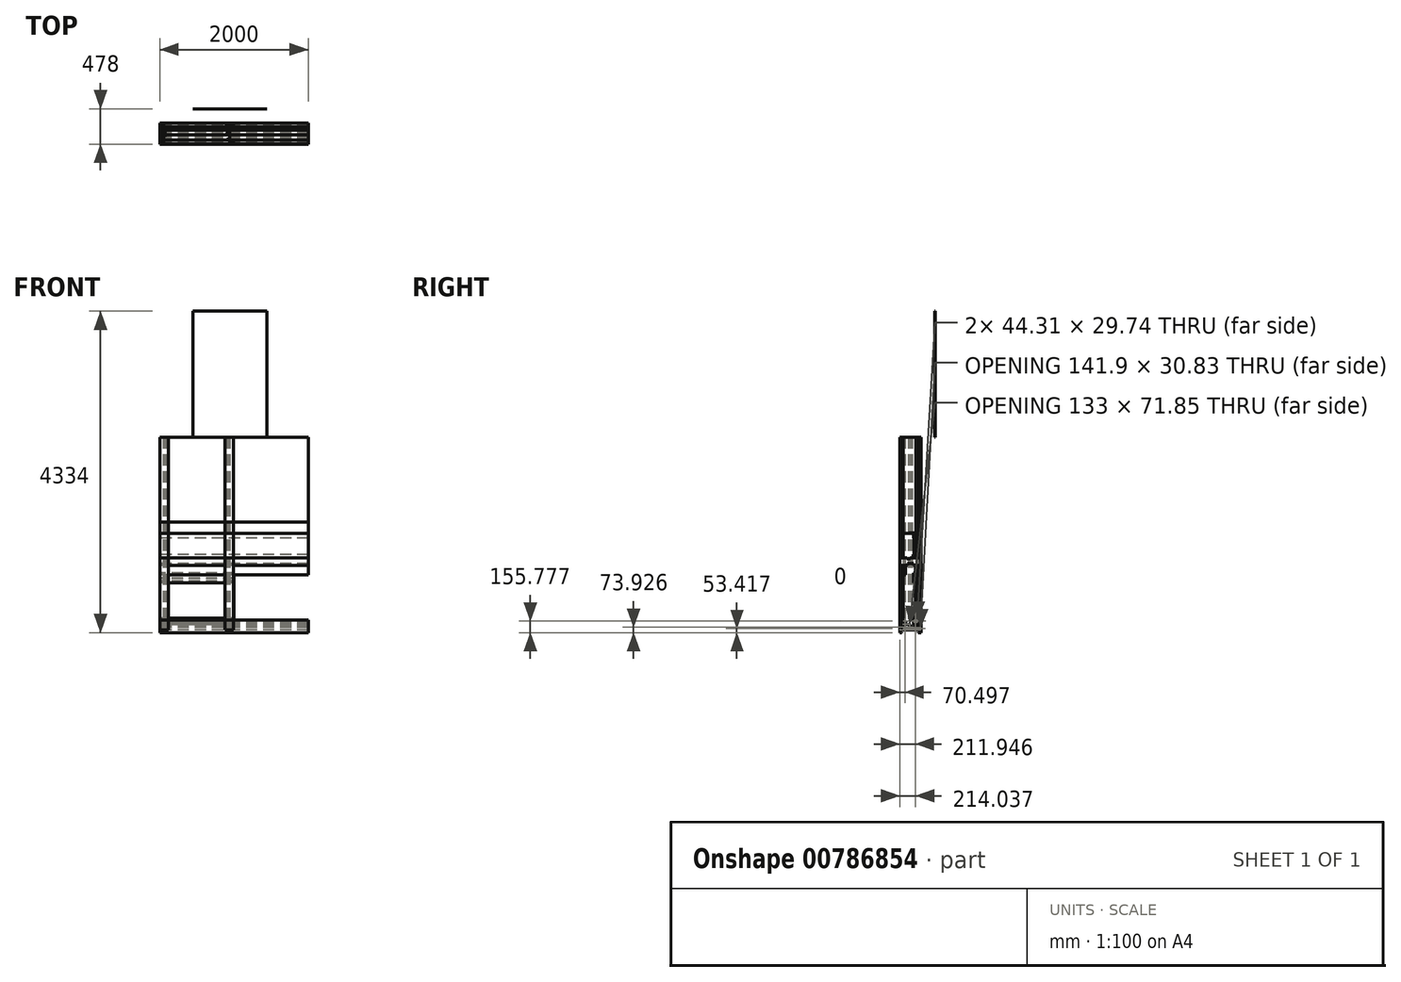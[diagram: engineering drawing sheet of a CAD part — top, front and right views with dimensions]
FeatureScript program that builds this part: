
annotation { "Feature Type Name" : "Feature", "Feature Type Description" : "" }
export const myFeature = defineFeature(function(context is Context, id is Id, definition is map)
    precondition{}
    {
        {
            var Q0;
            Q0=qCreatedBy(makeId("Top.planeOp"),FACE);
            var sketch = newSketch(context, id + "F0", { "sketchPlane" : qUnion([Q0])});
            skLineSegment(sketch, "E0", {"start": v(-131.77, 26.16) * mm, "end": v(-135.77, 26.16) * mm});
            skLineSegment(sketch, "E1", {"start": v(-135.77, 26.16) * mm, "end": v(-135.77, 70.16) * mm});
            skLineSegment(sketch, "E2", {"start": v(-135.77, 70.16) * mm, "end": v(-20.77, 70.16) * mm});
            skLineSegment(sketch, "E3", {"start": v(-20.77, 70.16) * mm, "end": v(-20.77, 66.16) * mm});
            skLineSegment(sketch, "E4", {"start": v(-20.77, 66.16) * mm, "end": v(-84.72, 66.16) * mm});
            skLineSegment(sketch, "E5", {"start": v(-84.72, 66.16) * mm, "end": v(-84.72, 4.73) * mm});
            skLineSegment(sketch, "E6", {"start": v(-84.72, 4.73) * mm, "end": v(-58.72, 4.73) * mm});
            skLineSegment(sketch, "E7", {"start": v(-58.72, 4.73) * mm, "end": v(-58.72, 6.73) * mm});
            skLineSegment(sketch, "E8", {"start": v(-58.72, 6.73) * mm, "end": v(-44.72, 0.73) * mm});
            skLineSegment(sketch, "E9", {"start": v(-44.72, 0.73) * mm, "end": v(-84.72, 0.73) * mm});
            skLineSegment(sketch, "E10", {"start": v(-84.72, 0.73) * mm, "end": v(-84.72, -93.45) * mm});
            skLineSegment(sketch, "E11", {"start": v(-84.72, -93.45) * mm, "end": v(-60.2, -93.45) * mm});
            skLineSegment(sketch, "E12", {"start": v(-60.2, -93.45) * mm, "end": v(-60.2, -73.83) * mm});
            skLineSegment(sketch, "E13", {"start": v(-60.2, -73.83) * mm, "end": v(-44.72, -73.83) * mm});
            skLineSegment(sketch, "E14", {"start": v(-44.72, -73.83) * mm, "end": v(-44.72, -79.83) * mm});
            skLineSegment(sketch, "E15", {"start": v(-44.72, -79.83) * mm, "end": v(-48.72, -79.83) * mm});
            skLineSegment(sketch, "E16", {"start": v(-48.72, -79.83) * mm, "end": v(-48.72, -77.83) * mm});
            skLineSegment(sketch, "E17", {"start": v(-48.72, -77.83) * mm, "end": v(-56.2, -77.83) * mm});
            skLineSegment(sketch, "E18", {"start": v(-56.2, -77.83) * mm, "end": v(-56.2, -93.45) * mm});
            skLineSegment(sketch, "E19", {"start": v(-56.2, -93.45) * mm, "end": v(-48.72, -93.45) * mm});
            skLineSegment(sketch, "E20", {"start": v(-48.72, -93.45) * mm, "end": v(-48.72, -91.45) * mm});
            skLineSegment(sketch, "E21", {"start": v(-48.72, -91.45) * mm, "end": v(-44.72, -91.45) * mm});
            skLineSegment(sketch, "E22", {"start": v(-44.72, -91.45) * mm, "end": v(-44.72, -97.45) * mm});
            skLineSegment(sketch, "E23", {"start": v(-44.72, -97.45) * mm, "end": v(-84.72, -97.45) * mm});
            skLineSegment(sketch, "E24", {"start": v(-84.72, -97.45) * mm, "end": v(-84.72, -212.73) * mm});
            skLineSegment(sketch, "E25", {"start": v(-84.72, -212.73) * mm, "end": v(-20.77, -212.73) * mm});
            skLineSegment(sketch, "E26", {"start": v(-20.77, -212.73) * mm, "end": v(-20.77, -216.73) * mm});
            skLineSegment(sketch, "E27", {"start": v(-20.77, -216.73) * mm, "end": v(-135.77, -216.73) * mm});
            skLineSegment(sketch, "E28", {"start": v(-135.77, -216.73) * mm, "end": v(-135.77, -172.73) * mm});
            skLineSegment(sketch, "E29", {"start": v(-135.77, -172.73) * mm, "end": v(-131.77, -172.73) * mm});
            skLineSegment(sketch, "E30", {"start": v(-131.77, -172.73) * mm, "end": v(-131.77, -212.73) * mm});
            skLineSegment(sketch, "E31", {"start": v(-131.77, -212.73) * mm, "end": v(-88.72, -212.73) * mm});
            skLineSegment(sketch, "E32", {"start": v(-88.72, -212.73) * mm, "end": v(-88.72, 66.16) * mm});
            skLineSegment(sketch, "E33", {"start": v(-88.72, 66.16) * mm, "end": v(-131.77, 66.16) * mm});
            skLineSegment(sketch, "E34", {"start": v(-131.77, 66.16) * mm, "end": v(-131.77, 26.16) * mm});
            skLineSegment(sketch, "E35.MirrorCS", {"start": v(763.76, -72.74) * mm, "end": v(763.76, -66.74) * mm});
            skLineSegment(sketch, "E36.MirrorCS", {"start": v(767.76, -66.74) * mm, "end": v(767.76, -68.74) * mm});
            skLineSegment(sketch, "E37.MirrorCS", {"start": v(767.76, -68.74) * mm, "end": v(775.23, -68.74) * mm});
            skLineSegment(sketch, "E38.MirrorCS", {"start": v(775.23, -68.74) * mm, "end": v(775.23, -53.12) * mm});
            skLineSegment(sketch, "E39.MirrorCS", {"start": v(779.23, -72.74) * mm, "end": v(763.76, -72.74) * mm});
            skLineSegment(sketch, "E40.MirrorCS", {"start": v(767.76, -53.12) * mm, "end": v(767.76, -55.12) * mm});
            skLineSegment(sketch, "E41.MirrorCS", {"start": v(763.76, -66.74) * mm, "end": v(767.76, -66.74) * mm});
            skLineSegment(sketch, "E42.MirrorCS", {"start": v(767.76, -55.12) * mm, "end": v(763.76, -55.12) * mm});
            skLineSegment(sketch, "E43.MirrorCS", {"start": v(763.76, -55.12) * mm, "end": v(763.76, -49.12) * mm});
            skLineSegment(sketch, "E44.MirrorCS", {"start": v(775.23, -53.12) * mm, "end": v(767.76, -53.12) * mm});
            skLineSegment(sketch, "E45.MirrorCS", {"start": v(779.23, -53.12) * mm, "end": v(779.23, -72.74) * mm});
            skLineSegment(sketch, "E46.MirrorCS", {"start": v(763.76, -49.12) * mm, "end": v(803.76, -49.12) * mm});
            skLineSegment(sketch, "E47.MirrorCS", {"start": v(803.76, -53.12) * mm, "end": v(779.23, -53.12) * mm});
            skLineSegment(sketch, "E48.MirrorCS", {"start": v(777.76, -153.3) * mm, "end": v(763.76, -147.3) * mm});
            skLineSegment(sketch, "E49.MirrorCS", {"start": v(850.81, -172.73) * mm, "end": v(854.81, -172.73) * mm});
            skLineSegment(sketch, "E50.MirrorCS", {"start": v(803.76, -151.3) * mm, "end": v(777.76, -151.3) * mm});
            skLineSegment(sketch, "E51.MirrorCS", {"start": v(777.76, -151.3) * mm, "end": v(777.76, -153.3) * mm});
            skLineSegment(sketch, "E52.MirrorCS", {"start": v(763.76, -147.3) * mm, "end": v(803.76, -147.3) * mm});
            skLineSegment(sketch, "E53.MirrorCS", {"start": v(739.81, -216.73) * mm, "end": v(739.81, -212.73) * mm});
            skLineSegment(sketch, "E54.MirrorCS", {"start": v(854.81, -0.01) * mm, "end": v(850.81, -0.01) * mm});
            skLineSegment(sketch, "E55.MirrorCS", {"start": v(739.81, 39.99) * mm, "end": v(739.81, 43.99) * mm});
            skLineSegment(sketch, "E56.MirrorCS", {"start": v(850.81, 39.99) * mm, "end": v(807.76, 39.99) * mm});
            skLineSegment(sketch, "E57.MirrorCS", {"start": v(803.76, -49.12) * mm, "end": v(803.76, 39.99) * mm});
            skLineSegment(sketch, "E58.MirrorCS", {"start": v(854.81, -172.73) * mm, "end": v(854.81, -216.73) * mm});
            skLineSegment(sketch, "E59.MirrorCS", {"start": v(807.76, -212.73) * mm, "end": v(850.81, -212.73) * mm});
            skLineSegment(sketch, "E60.MirrorCS", {"start": v(850.81, -0.01) * mm, "end": v(850.81, 39.99) * mm});
            skLineSegment(sketch, "E61.MirrorCS", {"start": v(854.81, -216.73) * mm, "end": v(739.81, -216.73) * mm});
            skLineSegment(sketch, "E62.MirrorCS", {"start": v(850.81, -212.73) * mm, "end": v(850.81, -172.73) * mm});
            skLineSegment(sketch, "E63.MirrorCS", {"start": v(803.76, 39.99) * mm, "end": v(739.81, 39.99) * mm});
            skLineSegment(sketch, "E64.MirrorCS", {"start": v(803.76, -147.3) * mm, "end": v(803.76, -53.12) * mm});
            skLineSegment(sketch, "E65.MirrorCS", {"start": v(803.76, -212.73) * mm, "end": v(803.76, -151.3) * mm});
            skLineSegment(sketch, "E66.MirrorCS", {"start": v(739.81, -212.73) * mm, "end": v(803.76, -212.73) * mm});
            skLineSegment(sketch, "E67.MirrorCS", {"start": v(854.81, 43.99) * mm, "end": v(854.81, -0.01) * mm});
            skLineSegment(sketch, "E68.MirrorCS", {"start": v(807.76, 39.99) * mm, "end": v(807.76, -212.73) * mm});
            skLineSegment(sketch, "E69.MirrorCS", {"start": v(739.81, 43.99) * mm, "end": v(854.81, 43.99) * mm});
            skSolve(sketch);
        }
        {
            var Q0;
            Q0=makeQuery(id+"F0.imprint","IMPRINT",FACE,{"disambiguationData":[TD([[makeQuery(id+"F0.imprint","IMPRINT",EDGE,{"derivedFrom":sQuery(id+"F0.wireOp",EDGE,"E0")}),-1.0]])]});
            extrude(context, id + "F1", {"entities" : qUnion([Q0]), "depth" : 2600 * mm, "offsetDistance" : 25 * mm});
        }
        {
            var Q0;
            Q0=makeQuery(id+"F0.imprint","IMPRINT",FACE,{"disambiguationData":[TD([[makeQuery(id+"F0.imprint","IMPRINT",EDGE,{"derivedFrom":sQuery(id+"F0.wireOp",EDGE,"E35.MirrorCS")}),-1.0]])]});
            extrude(context, id + "F2", {"entities" : qUnion([Q0]), "depth" : 2600 * mm, "offsetDistance" : 25 * mm});
        }
        {
            var Q0;
            Q0=makeQuery(id+"F1.opExtrude","SWEPT_FACE",FACE,{"disambiguationData":[OSD([sQuery(id+"F0.wireOp",EDGE,"E28")])]});
            var sketch = newSketch(context, id + "F3", { "sketchPlane" : qUnion([Q0])});
            skLineSegment(sketch, "E70", {"start": v(-70.16, -34) * mm, "end": v(-70.16, 69.03) * mm});
            skLineSegment(sketch, "E71", {"start": v(-70.16, 69.03) * mm, "end": v(-66.16, 69.03) * mm});
            skLineSegment(sketch, "E72", {"start": v(-66.16, 69.03) * mm, "end": v(-66.16, 36.25) * mm});
            skLineSegment(sketch, "E73", {"start": v(-66.16, 36.25) * mm, "end": v(-11.46, 36.25) * mm});
            skLineSegment(sketch, "E74", {"start": v(0, 38.83) * mm, "end": v(0, 88.3) * mm});
            skLineSegment(sketch, "E75", {"start": v(0, 88.3) * mm, "end": v(-6.87, 88.3) * mm});
            skLineSegment(sketch, "E76", {"start": v(-6.87, 88.3) * mm, "end": v(-6.87, 76.3) * mm});
            skLineSegment(sketch, "E77", {"start": v(-6.87, 76.3) * mm, "end": v(-11.46, 76.3) * mm});
            skLineSegment(sketch, "E78", {"start": v(-11.46, 76.3) * mm, "end": v(-11.46, 92.3) * mm});
            skLineSegment(sketch, "E79", {"start": v(-11.46, 92.3) * mm, "end": v(16.85, 92.3) * mm});
            skLineSegment(sketch, "E80", {"start": v(16.85, 92.3) * mm, "end": v(16.85, 76.3) * mm});
            skLineSegment(sketch, "E81", {"start": v(16.85, 76.3) * mm, "end": v(12.85, 76.3) * mm});
            skLineSegment(sketch, "E82", {"start": v(12.85, 76.3) * mm, "end": v(12.85, 88.3) * mm});
            skLineSegment(sketch, "E83", {"start": v(12.85, 88.3) * mm, "end": v(4, 88.3) * mm});
            skLineSegment(sketch, "E84", {"start": v(4, 88.3) * mm, "end": v(4, 38.83) * mm});
            skLineSegment(sketch, "E85", {"start": v(-70.16, -34) * mm, "end": v(-32.13, -34) * mm});
            skLineSegment(sketch, "E86", {"start": v(-32.13, -34) * mm, "end": v(-32.13, -30) * mm});
            skLineSegment(sketch, "E87", {"start": v(-32.13, -30) * mm, "end": v(-66.16, -30) * mm});
            skLineSegment(sketch, "E88", {"start": v(-66.16, -30) * mm, "end": v(-66.16, 0) * mm});
            skLineSegment(sketch, "E89", {"start": v(-66.16, 0) * mm, "end": v(212.73, 0) * mm});
            skLineSegment(sketch, "E90", {"start": v(212.73, -30) * mm, "end": v(187.57, -30) * mm});
            skLineSegment(sketch, "E91", {"start": v(187.57, -30) * mm, "end": v(187.57, -34) * mm});
            skLineSegment(sketch, "E92", {"start": v(187.57, -34) * mm, "end": v(216.73, -34) * mm});
            skLineSegment(sketch, "E93", {"start": v(216.73, -34) * mm, "end": v(216.73, 138.64) * mm});
            skLineSegment(sketch, "E94", {"start": v(216.73, 138.64) * mm, "end": v(212.73, 138.64) * mm});
            skLineSegment(sketch, "E95", {"start": v(212.73, 138.64) * mm, "end": v(212.73, 113.43) * mm});
            skLineSegment(sketch, "E96", {"start": v(212.73, 113.43) * mm, "end": v(206.73, 113.43) * mm});
            skLineSegment(sketch, "E97", {"start": v(206.73, 113.43) * mm, "end": v(206.73, 107.43) * mm});
            skLineSegment(sketch, "E98", {"start": v(206.73, 107.43) * mm, "end": v(210.73, 107.43) * mm});
            skLineSegment(sketch, "E99", {"start": v(210.73, 107.43) * mm, "end": v(210.73, 109.43) * mm});
            skLineSegment(sketch, "E100", {"start": v(210.73, 109.43) * mm, "end": v(212.73, 109.43) * mm});
            skLineSegment(sketch, "E101", {"start": v(212.73, 109.43) * mm, "end": v(212.73, 88) * mm});
            skLineSegment(sketch, "E102", {"start": v(212.73, 88) * mm, "end": v(210.73, 88) * mm});
            skLineSegment(sketch, "E103", {"start": v(210.73, 88) * mm, "end": v(210.73, 90) * mm});
            skLineSegment(sketch, "E104", {"start": v(210.73, 90) * mm, "end": v(206.73, 90) * mm});
            skLineSegment(sketch, "E105", {"start": v(206.73, 90) * mm, "end": v(206.73, 84) * mm});
            skLineSegment(sketch, "E106", {"start": v(206.73, 84) * mm, "end": v(212.73, 84) * mm});
            skLineSegment(sketch, "E107", {"start": v(212.73, 84) * mm, "end": v(212.73, 79.86) * mm});
            skLineSegment(sketch, "E108", {"start": v(212.73, -30) * mm, "end": v(212.73, 0) * mm});
            skLineSegment(sketch, "E109", {"start": v(212.73, 4) * mm, "end": v(79.73, 4) * mm});
            skLineSegment(sketch, "E110", {"start": v(72.84, 551.08) * mm, "end": v(72.84, 267.71) * mm, "construction": true});
            skLineSegment(sketch, "E111", {"start": v(146.73, 79.86) * mm, "end": v(146.73, 115.55) * mm});
            skLineSegment(sketch, "E112", {"start": v(150.73, 115.55) * mm, "end": v(150.73, 103.55) * mm});
            skLineSegment(sketch, "E113", {"start": v(150.73, 103.55) * mm, "end": v(154.73, 103.55) * mm});
            skLineSegment(sketch, "E114", {"start": v(154.73, 103.55) * mm, "end": v(154.73, 119.55) * mm});
            skLineSegment(sketch, "E115", {"start": v(154.73, 119.55) * mm, "end": v(134.73, 119.55) * mm});
            skLineSegment(sketch, "E116", {"start": v(134.73, 119.55) * mm, "end": v(134.73, 103.55) * mm});
            skLineSegment(sketch, "E117", {"start": v(134.73, 103.55) * mm, "end": v(138.73, 103.55) * mm});
            skLineSegment(sketch, "E118", {"start": v(138.73, 103.55) * mm, "end": v(138.73, 115.55) * mm});
            skLineSegment(sketch, "E119", {"start": v(138.73, 115.55) * mm, "end": v(142.73, 115.55) * mm});
            skLineSegment(sketch, "E120", {"start": v(142.73, 115.55) * mm, "end": v(142.73, 79.86) * mm});
            skLineSegment(sketch, "E121", {"start": v(142.73, 79.86) * mm, "end": v(67.73, 74.54) * mm});
            skLineSegment(sketch, "E122", {"start": v(67.73, 74.54) * mm, "end": v(67.73, 62.44) * mm});
            skLineSegment(sketch, "E123", {"start": v(67.73, 62.44) * mm, "end": v(71.73, 62.44) * mm});
            skLineSegment(sketch, "E124", {"start": v(71.73, 62.44) * mm, "end": v(71.73, 66.44) * mm});
            skLineSegment(sketch, "E125", {"start": v(71.73, 66.44) * mm, "end": v(75.73, 66.44) * mm});
            skLineSegment(sketch, "E126", {"start": v(75.73, 66.44) * mm, "end": v(75.73, 50.83) * mm});
            skLineSegment(sketch, "E127", {"start": v(75.73, 50.83) * mm, "end": v(71.73, 50.83) * mm});
            skLineSegment(sketch, "E128", {"start": v(71.73, 50.83) * mm, "end": v(71.73, 54.83) * mm});
            skLineSegment(sketch, "E129", {"start": v(71.73, 54.83) * mm, "end": v(67.73, 54.83) * mm});
            skLineSegment(sketch, "E130", {"start": v(67.73, 54.83) * mm, "end": v(67.73, 46.83) * mm});
            skLineSegment(sketch, "E131", {"start": v(67.73, 46.83) * mm, "end": v(75.73, 46.83) * mm});
            skLineSegment(sketch, "E132", {"start": v(75.73, 46.83) * mm, "end": v(75.73, 38.83) * mm});
            skLineSegment(sketch, "E133", {"start": v(75.73, 38.83) * mm, "end": v(4, 38.83) * mm});
            skLineSegment(sketch, "E134", {"start": v(146.73, 115.55) * mm, "end": v(150.73, 115.55) * mm});
            skLineSegment(sketch, "E135", {"start": v(146.73, 79.86) * mm, "end": v(212.73, 79.86) * mm});
            skLineSegment(sketch, "E136", {"start": v(212.73, 75.85) * mm, "end": v(142.73, 75.85) * mm});
            skLineSegment(sketch, "E137.trimOffspring", {"start": v(212.73, 75.85) * mm, "end": v(212.73, 4) * mm});
            skLineSegment(sketch, "E138", {"start": v(79.73, 71.38) * mm, "end": v(79.73, 4) * mm});
            skLineSegment(sketch, "E139", {"start": v(142.73, 75.85) * mm, "end": v(79.73, 71.38) * mm});
            skLineSegment(sketch, "E140", {"start": v(75.73, 4) * mm, "end": v(75.73, 34.83) * mm});
            skLineSegment(sketch, "E141", {"start": v(75.73, 34.83) * mm, "end": v(-0.59, 34.83) * mm});
            skLineSegment(sketch, "E142", {"start": v(-12.05, 32.25) * mm, "end": v(-66.16, 32.25) * mm});
            skLineSegment(sketch, "E143", {"start": v(-66.16, 32.25) * mm, "end": v(-66.16, 4) * mm});
            skLineSegment(sketch, "E144", {"start": v(-66.16, 4) * mm, "end": v(75.73, 4) * mm});
            skLineSegment(sketch, "E145", {"start": v(-11.46, 36.25) * mm, "end": v(0, 38.83) * mm});
            skLineSegment(sketch, "E146", {"start": v(-12.05, 32.25) * mm, "end": v(-0.59, 34.83) * mm});
            skSolve(sketch);
        }
        {
            var Q0;
            Q0=qSketchRegion(id+"F3",true);
            extrude(context, id + "F4", {"entities" : qUnion([Q0]), "oppositeDirection" : true, "depth" : 2000 * mm, "offsetDistance" : 25 * mm});
        }
        {
            var Q0;
            Q0=makeQuery(id+"F1.opExtrude","SWEPT_FACE",FACE,{"disambiguationData":[OSD([sQuery(id+"F0.wireOp",EDGE,"E1")])]});
            var sketch = newSketch(context, id + "F5", { "sketchPlane" : qUnion([Q0])});
            skLineSegment(sketch, "E147", {"start": v(-70.16, 972.5) * mm, "end": v(-70.16, 2600) * mm});
            skLineSegment(sketch, "E148", {"start": v(-70.16, 972.5) * mm, "end": v(-14.46, 972.5) * mm});
            skLineSegment(sketch, "E149", {"start": v(-14.46, 972.5) * mm, "end": v(-14.46, 1017.43) * mm});
            skLineSegment(sketch, "E150", {"start": v(-14.46, 1017.43) * mm, "end": v(-10.46, 1017.43) * mm});
            skLineSegment(sketch, "E151", {"start": v(-10.46, 1017.43) * mm, "end": v(-10.46, 972.5) * mm});
            skLineSegment(sketch, "E152", {"start": v(-10.46, 972.5) * mm, "end": v(30.91, 972.5) * mm});
            skLineSegment(sketch, "E153", {"start": v(72.28, 972.5) * mm, "end": v(72.28, 964.5) * mm});
            skLineSegment(sketch, "E154", {"start": v(72.28, 964.5) * mm, "end": v(116.6, 964.5) * mm});
            skLineSegment(sketch, "E155", {"start": v(116.6, 964.5) * mm, "end": v(116.6, 972.5) * mm});
            skLineSegment(sketch, "E156", {"start": v(116.6, 972.5) * mm, "end": v(216.73, 972.5) * mm});
            skLineSegment(sketch, "E157", {"start": v(216.73, 2600) * mm, "end": v(216.73, 972.5) * mm});
            skLineSegment(sketch, "E158", {"start": v(-70.16, 2600) * mm, "end": v(-66.16, 2600) * mm});
            skLineSegment(sketch, "E159", {"start": v(-66.16, 875.29) * mm, "end": v(-66.16, 2600) * mm});
            skLineSegment(sketch, "E160", {"start": v(-66.16, 875.29) * mm, "end": v(1.84, 875.29) * mm});
            skLineSegment(sketch, "E161", {"start": v(1.84, 875.29) * mm, "end": v(1.84, 748.56) * mm});
            skLineSegment(sketch, "E162", {"start": v(1.84, 748.56) * mm, "end": v(5.84, 748.56) * mm});
            skLineSegment(sketch, "E163", {"start": v(5.84, 748.56) * mm, "end": v(5.84, 875.29) * mm});
            skLineSegment(sketch, "E164", {"start": v(5.84, 875.29) * mm, "end": v(33.47, 875.29) * mm});
            skLineSegment(sketch, "E165", {"start": v(33.47, 875.29) * mm, "end": v(33.47, 898.4) * mm});
            skLineSegment(sketch, "E166", {"start": v(33.47, 898.4) * mm, "end": v(112.2, 898.4) * mm});
            skLineSegment(sketch, "E167", {"start": v(30.91, 972.5) * mm, "end": v(30.91, 1017.1) * mm});
            skLineSegment(sketch, "E168", {"start": v(30.91, 1017.1) * mm, "end": v(34.91, 1017.1) * mm});
            skLineSegment(sketch, "E169", {"start": v(34.91, 1017.1) * mm, "end": v(34.91, 972.5) * mm});
            skLineSegment(sketch, "E170.trimOffspring", {"start": v(34.91, 972.5) * mm, "end": v(72.28, 972.5) * mm});
            skLineSegment(sketch, "E171", {"start": v(-66.16, 879.29) * mm, "end": v(-66.16, 968.5) * mm});
            skLineSegment(sketch, "E172", {"start": v(-66.16, 968.5) * mm, "end": v(68.28, 968.5) * mm});
            skLineSegment(sketch, "E173", {"start": v(68.28, 968.5) * mm, "end": v(68.28, 960.5) * mm});
            skLineSegment(sketch, "E174", {"start": v(68.28, 960.5) * mm, "end": v(120.6, 960.5) * mm});
            skLineSegment(sketch, "E175", {"start": v(120.6, 960.5) * mm, "end": v(120.6, 966.67) * mm});
            skLineSegment(sketch, "E176", {"start": v(120.6, 966.67) * mm, "end": v(212.73, 966.67) * mm});
            skLineSegment(sketch, "E177", {"start": v(212.73, 966.67) * mm, "end": v(212.73, 879.29) * mm});
            skLineSegment(sketch, "E178", {"start": v(-66.16, 879.29) * mm, "end": v(29.47, 879.29) * mm});
            skLineSegment(sketch, "E179", {"start": v(29.47, 879.29) * mm, "end": v(29.47, 902.4) * mm});
            skLineSegment(sketch, "E180", {"start": v(29.47, 902.4) * mm, "end": v(116.2, 902.4) * mm});
            skLineSegment(sketch, "E181.MirrorCS", {"start": v(112.2, 875.29) * mm, "end": v(112.2, 898.4) * mm});
            skLineSegment(sketch, "E182.MirrorCS", {"start": v(116.2, 879.29) * mm, "end": v(116.2, 902.4) * mm});
            skLineSegment(sketch, "E183.MirrorCS", {"start": v(211.84, 879.29) * mm, "end": v(116.2, 879.29) * mm});
            skLineSegment(sketch, "E184.MirrorCS", {"start": v(211.84, 875.29) * mm, "end": v(143.84, 875.29) * mm});
            skLineSegment(sketch, "E185.MirrorCS", {"start": v(143.84, 748.56) * mm, "end": v(139.84, 748.56) * mm});
            skLineSegment(sketch, "E186.MirrorCS", {"start": v(139.84, 748.56) * mm, "end": v(139.84, 875.29) * mm});
            skLineSegment(sketch, "E187.MirrorCS", {"start": v(143.84, 875.29) * mm, "end": v(143.84, 748.56) * mm});
            skLineSegment(sketch, "E188.MirrorCS", {"start": v(139.84, 875.29) * mm, "end": v(112.2, 875.29) * mm});
            skLineSegment(sketch, "E189", {"start": v(216.73, 2600) * mm, "end": v(212.73, 2600) * mm});
            skLineSegment(sketch, "E190", {"start": v(212.73, 875.29) * mm, "end": v(212.73, 2600) * mm});
            skLineSegment(sketch, "E191", {"start": v(211.84, 879.29) * mm, "end": v(212.73, 879.29) * mm});
            skLineSegment(sketch, "E192", {"start": v(211.84, 875.29) * mm, "end": v(212.73, 875.29) * mm});
            skSolve(sketch);
        }
        {
            var Q0;
            Q0=qSketchRegion(id+"F5",true);
            extrude(context, id + "F6", {"entities" : qUnion([Q0]), "oppositeDirection" : true, "depth" : 2000 * mm, "offsetDistance" : 25 * mm});
        }
        {
            var Q0;
            Q0=makeQuery(id+"F6.opExtrude","CAP_FACE",FACE,{"disambiguationData":[OSD([sQuery(id+"F5.wireOp",EDGE,"E147"),sQuery(id+"F5.wireOp",EDGE,"E148"),sQuery(id+"F5.wireOp",EDGE,"E149"),sQuery(id+"F5.wireOp",EDGE,"E150"),sQuery(id+"F5.wireOp",EDGE,"E151"),sQuery(id+"F5.wireOp",EDGE,"E152"),sQuery(id+"F5.wireOp",EDGE,"E153"),sQuery(id+"F5.wireOp",EDGE,"E154"),sQuery(id+"F5.wireOp",EDGE,"E155"),sQuery(id+"F5.wireOp",EDGE,"E156"),sQuery(id+"F5.wireOp",EDGE,"E157"),sQuery(id+"F5.wireOp",EDGE,"E158"),sQuery(id+"F5.wireOp",EDGE,"E159"),sQuery(id+"F5.wireOp",EDGE,"E160"),sQuery(id+"F5.wireOp",EDGE,"E161"),sQuery(id+"F5.wireOp",EDGE,"E162"),sQuery(id+"F5.wireOp",EDGE,"E163"),sQuery(id+"F5.wireOp",EDGE,"E164"),sQuery(id+"F5.wireOp",EDGE,"E165"),sQuery(id+"F5.wireOp",EDGE,"E166"),sQuery(id+"F5.wireOp",EDGE,"E167"),sQuery(id+"F5.wireOp",EDGE,"E168"),sQuery(id+"F5.wireOp",EDGE,"E169"),sQuery(id+"F5.wireOp",EDGE,"E170.trimOffspring"),sQuery(id+"F5.wireOp",EDGE,"E171"),sQuery(id+"F5.wireOp",EDGE,"E172"),sQuery(id+"F5.wireOp",EDGE,"E173"),sQuery(id+"F5.wireOp",EDGE,"E174"),sQuery(id+"F5.wireOp",EDGE,"E175"),sQuery(id+"F5.wireOp",EDGE,"E176"),sQuery(id+"F5.wireOp",EDGE,"E177"),sQuery(id+"F5.wireOp",EDGE,"E178"),sQuery(id+"F5.wireOp",EDGE,"E179"),sQuery(id+"F5.wireOp",EDGE,"E180"),sQuery(id+"F5.wireOp",EDGE,"E181.MirrorCS"),sQuery(id+"F5.wireOp",EDGE,"E182.MirrorCS"),sQuery(id+"F5.wireOp",EDGE,"E183.MirrorCS"),sQuery(id+"F5.wireOp",EDGE,"E184.MirrorCS"),sQuery(id+"F5.wireOp",EDGE,"E185.MirrorCS"),sQuery(id+"F5.wireOp",EDGE,"E186.MirrorCS"),sQuery(id+"F5.wireOp",EDGE,"E187.MirrorCS"),sQuery(id+"F5.wireOp",EDGE,"E188.MirrorCS"),sQuery(id+"F5.wireOp",EDGE,"E189"),sQuery(id+"F5.wireOp",EDGE,"E190"),sQuery(id+"F5.wireOp",EDGE,"E191"),sQuery(id+"F5.wireOp",EDGE,"E192")])],"isStart":true});
            var sketch = newSketch(context, id + "F7", { "sketchPlane" : qUnion([Q0])});
            skLineSegment(sketch, "E193", {"start": v(-10.46, 1243.09) * mm, "end": v(-10.46, 1302.74) * mm});
            skLineSegment(sketch, "E194", {"start": v(-10.46, 1302.74) * mm, "end": v(26.58, 1302.74) * mm});
            skLineSegment(sketch, "E195", {"start": v(30.91, 1302.74) * mm, "end": v(30.91, 1306.74) * mm});
            skLineSegment(sketch, "E196", {"start": v(30.91, 1306.74) * mm, "end": v(87.31, 1306.74) * mm});
            skLineSegment(sketch, "E197", {"start": v(87.31, 1306.74) * mm, "end": v(87.31, 1302.74) * mm});
            skLineSegment(sketch, "E198", {"start": v(87.31, 1302.74) * mm, "end": v(216.73, 1302.74) * mm});
            skLineSegment(sketch, "E199", {"start": v(216.73, 1302.74) * mm, "end": v(216.73, 1459.6) * mm});
            skLineSegment(sketch, "E200", {"start": v(216.73, 1459.6) * mm, "end": v(160.6, 1459.6) * mm});
            skLineSegment(sketch, "E201", {"start": v(160.6, 1459.6) * mm, "end": v(160.6, 1455.6) * mm});
            skLineSegment(sketch, "E202", {"start": v(160.6, 1455.6) * mm, "end": v(212.73, 1455.6) * mm});
            skLineSegment(sketch, "E203", {"start": v(212.73, 1455.6) * mm, "end": v(212.73, 1306.74) * mm});
            skLineSegment(sketch, "E204", {"start": v(212.73, 1306.74) * mm, "end": v(91.31, 1306.74) * mm});
            skLineSegment(sketch, "E205", {"start": v(91.31, 1306.74) * mm, "end": v(91.31, 1310.74) * mm});
            skLineSegment(sketch, "E206", {"start": v(91.31, 1310.74) * mm, "end": v(26.91, 1310.74) * mm});
            skLineSegment(sketch, "E207", {"start": v(26.91, 1310.74) * mm, "end": v(26.91, 1306.74) * mm});
            skLineSegment(sketch, "E208", {"start": v(30.91, 1243.09) * mm, "end": v(30.91, 1302.74) * mm});
            skLineSegment(sketch, "E209", {"start": v(-10.46, 1243.09) * mm, "end": v(-14.46, 1243.09) * mm});
            skLineSegment(sketch, "E210", {"start": v(-14.46, 1243.09) * mm, "end": v(-14.46, 1302.74) * mm});
            skLineSegment(sketch, "E211", {"start": v(-14.46, 1302.74) * mm, "end": v(-70.16, 1302.74) * mm});
            skLineSegment(sketch, "E212", {"start": v(-70.16, 1302.74) * mm, "end": v(-70.16, 1458.04) * mm});
            skLineSegment(sketch, "E213", {"start": v(-70.16, 1458.04) * mm, "end": v(-14.46, 1458.04) * mm});
            skLineSegment(sketch, "E214", {"start": v(-14.46, 1458.04) * mm, "end": v(-14.46, 1454.04) * mm});
            skLineSegment(sketch, "E215", {"start": v(-14.46, 1454.04) * mm, "end": v(-66.16, 1454.04) * mm});
            skLineSegment(sketch, "E216", {"start": v(-66.16, 1454.04) * mm, "end": v(-66.16, 1306.74) * mm});
            skLineSegment(sketch, "E217", {"start": v(-66.16, 1306.74) * mm, "end": v(0, 1306.74) * mm});
            skLineSegment(sketch, "E218", {"start": v(0, 1306.74) * mm, "end": v(26.91, 1306.74) * mm});
            skLineSegment(sketch, "E219", {"start": v(30.91, 1243.09) * mm, "end": v(26.58, 1243.09) * mm});
            skLineSegment(sketch, "E220", {"start": v(26.58, 1243.09) * mm, "end": v(26.58, 1302.74) * mm});
            skSolve(sketch);
        }
        {
            var Q0;
            Q0=qSketchRegion(id+"F7",true);
            extrude(context, id + "F8", {"entities" : qUnion([Q0]), "oppositeDirection" : true, "depth" : 2000 * mm, "offsetDistance" : 25 * mm});
        }
        {
            var Q0;
            Q0=makeQuery(id+"F8.opExtrude","CAP_FACE",FACE,{"disambiguationData":[OSD([sQuery(id+"F7.wireOp",EDGE,"E193"),sQuery(id+"F7.wireOp",EDGE,"E194"),sQuery(id+"F7.wireOp",EDGE,"E195"),sQuery(id+"F7.wireOp",EDGE,"E196"),sQuery(id+"F7.wireOp",EDGE,"E197"),sQuery(id+"F7.wireOp",EDGE,"E198"),sQuery(id+"F7.wireOp",EDGE,"E199"),sQuery(id+"F7.wireOp",EDGE,"E200"),sQuery(id+"F7.wireOp",EDGE,"E201"),sQuery(id+"F7.wireOp",EDGE,"E202"),sQuery(id+"F7.wireOp",EDGE,"E203"),sQuery(id+"F7.wireOp",EDGE,"E204"),sQuery(id+"F7.wireOp",EDGE,"E205"),sQuery(id+"F7.wireOp",EDGE,"E206"),sQuery(id+"F7.wireOp",EDGE,"E207"),sQuery(id+"F7.wireOp",EDGE,"E208"),sQuery(id+"F7.wireOp",EDGE,"E209"),sQuery(id+"F7.wireOp",EDGE,"E210"),sQuery(id+"F7.wireOp",EDGE,"E211"),sQuery(id+"F7.wireOp",EDGE,"E212"),sQuery(id+"F7.wireOp",EDGE,"E213"),sQuery(id+"F7.wireOp",EDGE,"E214"),sQuery(id+"F7.wireOp",EDGE,"E215"),sQuery(id+"F7.wireOp",EDGE,"E216"),sQuery(id+"F7.wireOp",EDGE,"E217"),sQuery(id+"F7.wireOp",EDGE,"E218"),sQuery(id+"F7.wireOp",EDGE,"E219"),sQuery(id+"F7.wireOp",EDGE,"E220")])],"isStart":true});
            var sketch = newSketch(context, id + "F9", { "sketchPlane" : qUnion([Q0])});
            skLineSegment(sketch, "E221.bottom", {"start": v(-7.73, 1292.73) * mm, "end": v(24.3, 1292.73) * mm});
            skLineSegment(sketch, "E221.top", {"start": v(-7.73, 977.48) * mm, "end": v(24.3, 977.48) * mm});
            skLineSegment(sketch, "E221.left", {"start": v(-7.73, 1292.73) * mm, "end": v(-7.73, 977.48) * mm});
            skLineSegment(sketch, "E221.right", {"start": v(24.3, 1292.73) * mm, "end": v(24.3, 977.48) * mm});
            skSolve(sketch);
        }
        {
            var Q0;
            Q0=makeQuery(id+"F9.imprint","IMPRINT",FACE,{"disambiguationData":[TD([[makeQuery(id+"F9.imprint","IMPRINT",EDGE,{"derivedFrom":sQuery(id+"F9.wireOp",EDGE,"E221.bottom")}),-1.0]])]});
            extrude(context, id + "F10", {"entities" : qUnion([Q0]), "oppositeDirection" : true, "depth" : 2000 * mm, "offsetDistance" : 25 * mm});
        }
        {
            var Q0;
            Q0=makeQuery(id+"F6.opExtrude","CAP_FACE",FACE,{"disambiguationData":[OSD([sQuery(id+"F5.wireOp",EDGE,"E148"),sQuery(id+"F5.wireOp",EDGE,"E149"),sQuery(id+"F5.wireOp",EDGE,"E150"),sQuery(id+"F5.wireOp",EDGE,"E151"),sQuery(id+"F5.wireOp",EDGE,"E152"),sQuery(id+"F5.wireOp",EDGE,"E153"),sQuery(id+"F5.wireOp",EDGE,"E154"),sQuery(id+"F5.wireOp",EDGE,"E155"),sQuery(id+"F5.wireOp",EDGE,"E156"),sQuery(id+"F5.wireOp",EDGE,"E159"),sQuery(id+"F5.wireOp",EDGE,"E160"),sQuery(id+"F5.wireOp",EDGE,"E161"),sQuery(id+"F5.wireOp",EDGE,"E162"),sQuery(id+"F5.wireOp",EDGE,"E163"),sQuery(id+"F5.wireOp",EDGE,"E164"),sQuery(id+"F5.wireOp",EDGE,"E165"),sQuery(id+"F5.wireOp",EDGE,"E166"),sQuery(id+"F5.wireOp",EDGE,"E167"),sQuery(id+"F5.wireOp",EDGE,"E168"),sQuery(id+"F5.wireOp",EDGE,"E169"),sQuery(id+"F5.wireOp",EDGE,"E170.trimOffspring"),sQuery(id+"F5.wireOp",EDGE,"E171"),sQuery(id+"F5.wireOp",EDGE,"E181.MirrorCS"),sQuery(id+"F5.wireOp",EDGE,"E184.MirrorCS"),sQuery(id+"F5.wireOp",EDGE,"E185.MirrorCS"),sQuery(id+"F5.wireOp",EDGE,"E186.MirrorCS"),sQuery(id+"F5.wireOp",EDGE,"E187.MirrorCS"),sQuery(id+"F5.wireOp",EDGE,"E188.MirrorCS"),sQuery(id+"F5.wireOp",EDGE,"E190"),sQuery(id+"F5.wireOp",EDGE,"E192")])],"isStart":true});
            var sketch = newSketch(context, id + "F11", { "sketchPlane" : qUnion([Q0])});
            skLineSegment(sketch, "E222", {"start": v(-8.81, 768.15) * mm, "end": v(-20.84, 768.15) * mm});
            skLineSegment(sketch, "E223", {"start": v(-20.84, 768.15) * mm, "end": v(-20.84, 638.71) * mm});
            skLineSegment(sketch, "E224", {"start": v(-20.84, 638.71) * mm, "end": v(-3.18, 638.71) * mm});
            skLineSegment(sketch, "E225", {"start": v(-3.18, 638.71) * mm, "end": v(-3.18, 661.2) * mm});
            skLineSegment(sketch, "E226", {"start": v(-3.18, 661.2) * mm, "end": v(-7.18, 661.2) * mm});
            skLineSegment(sketch, "E227", {"start": v(-7.18, 661.2) * mm, "end": v(-7.18, 643.15) * mm});
            skLineSegment(sketch, "E228", {"start": v(-7.18, 643.15) * mm, "end": v(-16.84, 643.15) * mm});
            skLineSegment(sketch, "E229", {"start": v(-16.84, 643.15) * mm, "end": v(-16.84, 694.48) * mm});
            skLineSegment(sketch, "E230", {"start": v(28.61, 638.71) * mm, "end": v(7.9, 638.94) * mm});
            skLineSegment(sketch, "E231", {"start": v(11.9, 643.93) * mm, "end": v(24.61, 643.87) * mm});
            skLineSegment(sketch, "E232", {"start": v(24.61, 643.87) * mm, "end": v(24.61, 694.48) * mm});
            skLineSegment(sketch, "E233", {"start": v(-16.84, 747.73) * mm, "end": v(-8.81, 747.73) * mm});
            skLineSegment(sketch, "E234", {"start": v(-8.81, 762.18) * mm, "end": v(-12.81, 762.18) * mm});
            skLineSegment(sketch, "E235", {"start": v(-12.81, 751.73) * mm, "end": v(-16.84, 751.73) * mm});
            skLineSegment(sketch, "E236", {"start": v(-16.84, 764.15) * mm, "end": v(-12.81, 764.15) * mm});
            skLineSegment(sketch, "E237", {"start": v(-12.81, 754.18) * mm, "end": v(-8.81, 754.18) * mm});
            skLineSegment(sketch, "E238", {"start": v(-16.84, 698.48) * mm, "end": v(24.61, 698.48) * mm});
            skLineSegment(sketch, "E239", {"start": v(24.61, 694.48) * mm, "end": v(-16.84, 694.48) * mm});
            skLineSegment(sketch, "E240.trimOffspring", {"start": v(-16.84, 698.48) * mm, "end": v(-16.84, 747.73) * mm});
            skLineSegment(sketch, "E241", {"start": v(24.61, 698.48) * mm, "end": v(24.61, 747.72) * mm});
            skLineSegment(sketch, "E242", {"start": v(24.61, 747.72) * mm, "end": v(16.61, 747.72) * mm});
            skLineSegment(sketch, "E243", {"start": v(16.61, 747.72) * mm, "end": v(16.61, 752.15) * mm});
            skLineSegment(sketch, "E244", {"start": v(16.61, 752.15) * mm, "end": v(20.61, 752.15) * mm});
            skLineSegment(sketch, "E245", {"start": v(24.61, 752.15) * mm, "end": v(24.61, 760.15) * mm});
            skLineSegment(sketch, "E246", {"start": v(20.61, 760.15) * mm, "end": v(16.61, 760.15) * mm});
            skLineSegment(sketch, "E247", {"start": v(16.61, 760.15) * mm, "end": v(16.61, 768.15) * mm});
            skLineSegment(sketch, "E248", {"start": v(16.61, 768.15) * mm, "end": v(28.61, 768.15) * mm});
            skLineSegment(sketch, "E249", {"start": v(20.61, 760.15) * mm, "end": v(20.61, 764.15) * mm});
            skLineSegment(sketch, "E250", {"start": v(20.61, 764.15) * mm, "end": v(24.61, 764.15) * mm});
            skLineSegment(sketch, "E251", {"start": v(24.61, 764.15) * mm, "end": v(24.61, 760.15) * mm});
            skLineSegment(sketch, "E252", {"start": v(24.61, 752.15) * mm, "end": v(24.61, 750.2) * mm});
            skLineSegment(sketch, "E253", {"start": v(24.61, 750.2) * mm, "end": v(20.61, 750.2) * mm});
            skLineSegment(sketch, "E254", {"start": v(20.61, 750.2) * mm, "end": v(20.61, 752.15) * mm});
            skLineSegment(sketch, "E255", {"start": v(-8.81, 768.15) * mm, "end": v(-8.81, 762.18) * mm});
            skLineSegment(sketch, "E256", {"start": v(-8.81, 754.18) * mm, "end": v(-8.81, 747.73) * mm});
            skLineSegment(sketch, "E257", {"start": v(-12.81, 764.15) * mm, "end": v(-12.81, 762.18) * mm});
            skLineSegment(sketch, "E258", {"start": v(-12.81, 754.18) * mm, "end": v(-12.81, 751.73) * mm});
            skLineSegment(sketch, "E259", {"start": v(-16.84, 764.15) * mm, "end": v(-16.84, 751.73) * mm});
            skLineSegment(sketch, "E260", {"start": v(28.61, 768.15) * mm, "end": v(28.61, 638.71) * mm});
            skLineSegment(sketch, "E261", {"start": v(7.9, 638.94) * mm, "end": v(7.9, 661.2) * mm});
            skLineSegment(sketch, "E262", {"start": v(7.9, 661.2) * mm, "end": v(11.9, 661.2) * mm});
            skLineSegment(sketch, "E263", {"start": v(11.9, 661.2) * mm, "end": v(11.9, 643.93) * mm});
            skSolve(sketch);
        }
        {
            var Q0;
            Q0=qSketchRegion(id+"F11",true);
            extrude(context, id + "F12", {"entities" : qUnion([Q0]), "oppositeDirection" : true, "depth" : 1000 * mm, "offsetDistance" : 25 * mm});
        }
        {
            var Q0;
            Q0=makeQuery(id+"F4.opExtrude","CAP_FACE",FACE,{"disambiguationData":[OSD([sQuery(id+"F3.wireOp",EDGE,"E70"),sQuery(id+"F3.wireOp",EDGE,"E71"),sQuery(id+"F3.wireOp",EDGE,"E72"),sQuery(id+"F3.wireOp",EDGE,"E73"),sQuery(id+"F3.wireOp",EDGE,"E74"),sQuery(id+"F3.wireOp",EDGE,"E75"),sQuery(id+"F3.wireOp",EDGE,"E76"),sQuery(id+"F3.wireOp",EDGE,"E77"),sQuery(id+"F3.wireOp",EDGE,"E78"),sQuery(id+"F3.wireOp",EDGE,"E79"),sQuery(id+"F3.wireOp",EDGE,"E80"),sQuery(id+"F3.wireOp",EDGE,"E81"),sQuery(id+"F3.wireOp",EDGE,"E82"),sQuery(id+"F3.wireOp",EDGE,"E83"),sQuery(id+"F3.wireOp",EDGE,"E84"),sQuery(id+"F3.wireOp",EDGE,"E85"),sQuery(id+"F3.wireOp",EDGE,"E86"),sQuery(id+"F3.wireOp",EDGE,"E87"),sQuery(id+"F3.wireOp",EDGE,"E88"),sQuery(id+"F3.wireOp",EDGE,"E89"),sQuery(id+"F3.wireOp",EDGE,"E90"),sQuery(id+"F3.wireOp",EDGE,"E91"),sQuery(id+"F3.wireOp",EDGE,"E92"),sQuery(id+"F3.wireOp",EDGE,"E93"),sQuery(id+"F3.wireOp",EDGE,"E94"),sQuery(id+"F3.wireOp",EDGE,"E95"),sQuery(id+"F3.wireOp",EDGE,"E96"),sQuery(id+"F3.wireOp",EDGE,"E97"),sQuery(id+"F3.wireOp",EDGE,"E98"),sQuery(id+"F3.wireOp",EDGE,"E99"),sQuery(id+"F3.wireOp",EDGE,"E100"),sQuery(id+"F3.wireOp",EDGE,"E101"),sQuery(id+"F3.wireOp",EDGE,"E102"),sQuery(id+"F3.wireOp",EDGE,"E103"),sQuery(id+"F3.wireOp",EDGE,"E104"),sQuery(id+"F3.wireOp",EDGE,"E105"),sQuery(id+"F3.wireOp",EDGE,"E106"),sQuery(id+"F3.wireOp",EDGE,"E107"),sQuery(id+"F3.wireOp",EDGE,"E108"),sQuery(id+"F3.wireOp",EDGE,"E109"),sQuery(id+"F3.wireOp",EDGE,"E111"),sQuery(id+"F3.wireOp",EDGE,"E112"),sQuery(id+"F3.wireOp",EDGE,"E113"),sQuery(id+"F3.wireOp",EDGE,"E114"),sQuery(id+"F3.wireOp",EDGE,"E115"),sQuery(id+"F3.wireOp",EDGE,"E116"),sQuery(id+"F3.wireOp",EDGE,"E117"),sQuery(id+"F3.wireOp",EDGE,"E118"),sQuery(id+"F3.wireOp",EDGE,"E119"),sQuery(id+"F3.wireOp",EDGE,"E120"),sQuery(id+"F3.wireOp",EDGE,"E121"),sQuery(id+"F3.wireOp",EDGE,"E122"),sQuery(id+"F3.wireOp",EDGE,"E123"),sQuery(id+"F3.wireOp",EDGE,"E124"),sQuery(id+"F3.wireOp",EDGE,"E125"),sQuery(id+"F3.wireOp",EDGE,"E126"),sQuery(id+"F3.wireOp",EDGE,"E127"),sQuery(id+"F3.wireOp",EDGE,"E128"),sQuery(id+"F3.wireOp",EDGE,"E129"),sQuery(id+"F3.wireOp",EDGE,"E130"),sQuery(id+"F3.wireOp",EDGE,"E131"),sQuery(id+"F3.wireOp",EDGE,"E132"),sQuery(id+"F3.wireOp",EDGE,"E133"),sQuery(id+"F3.wireOp",EDGE,"E134"),sQuery(id+"F3.wireOp",EDGE,"E135"),sQuery(id+"F3.wireOp",EDGE,"E136"),sQuery(id+"F3.wireOp",EDGE,"E137.trimOffspring"),sQuery(id+"F3.wireOp",EDGE,"E138"),sQuery(id+"F3.wireOp",EDGE,"E139"),sQuery(id+"F3.wireOp",EDGE,"E140"),sQuery(id+"F3.wireOp",EDGE,"E141"),sQuery(id+"F3.wireOp",EDGE,"E142"),sQuery(id+"F3.wireOp",EDGE,"E143"),sQuery(id+"F3.wireOp",EDGE,"E144"),sQuery(id+"F3.wireOp",EDGE,"E145"),sQuery(id+"F3.wireOp",EDGE,"E146")])],"isStart":true});
            var sketch = newSketch(context, id + "F13", { "sketchPlane" : qUnion([Q0])});
            skLineSegment(sketch, "E264", {"start": v(-11.46, 78.29) * mm, "end": v(-11.46, 70.29) * mm});
            skLineSegment(sketch, "E265", {"start": v(-11.46, 70.29) * mm, "end": v(-23.46, 70.29) * mm});
            skLineSegment(sketch, "E266", {"start": v(-23.46, 70.29) * mm, "end": v(-23.46, 163.36) * mm});
            skLineSegment(sketch, "E267", {"start": v(-7, 150.71) * mm, "end": v(-3, 150.77) * mm});
            skLineSegment(sketch, "E268", {"start": v(-7, 150.71) * mm, "end": v(-7, 159.36) * mm});
            skLineSegment(sketch, "E269", {"start": v(-7, 159.36) * mm, "end": v(-19.46, 159.36) * mm});
            skLineSegment(sketch, "E270", {"start": v(-19.46, 159.36) * mm, "end": v(-19.46, 140.65) * mm});
            skLineSegment(sketch, "E271", {"start": v(-19.46, 140.65) * mm, "end": v(24.85, 140.65) * mm});
            skLineSegment(sketch, "E272", {"start": v(24.85, 140.65) * mm, "end": v(24.85, 159.36) * mm});
            skLineSegment(sketch, "E273", {"start": v(24.85, 159.36) * mm, "end": v(11, 159.36) * mm});
            skLineSegment(sketch, "E274", {"start": v(7, 163.36) * mm, "end": v(28.85, 163.36) * mm});
            skLineSegment(sketch, "E275", {"start": v(28.85, 163.36) * mm, "end": v(28.85, 70.29) * mm});
            skLineSegment(sketch, "E276", {"start": v(28.85, 70.29) * mm, "end": v(16.85, 70.29) * mm});
            skLineSegment(sketch, "E277", {"start": v(16.85, 70.29) * mm, "end": v(16.85, 78.29) * mm});
            skLineSegment(sketch, "E278", {"start": v(16.85, 78.29) * mm, "end": v(20.85, 78.29) * mm});
            skLineSegment(sketch, "E279.bottom", {"start": v(-19.46, 136.65) * mm, "end": v(24.85, 136.65) * mm});
            skLineSegment(sketch, "E279.top", {"start": v(-19.46, 106.9) * mm, "end": v(24.85, 106.9) * mm});
            skLineSegment(sketch, "E279.left", {"start": v(-19.46, 136.65) * mm, "end": v(-19.46, 106.9) * mm});
            skLineSegment(sketch, "E279.right", {"start": v(24.85, 136.65) * mm, "end": v(24.85, 106.9) * mm});
            skLineSegment(sketch, "E280", {"start": v(-11.46, 78.29) * mm, "end": v(-15.46, 78.29) * mm});
            skLineSegment(sketch, "E281", {"start": v(-15.46, 78.29) * mm, "end": v(-15.46, 74.29) * mm});
            skLineSegment(sketch, "E282", {"start": v(-15.46, 74.29) * mm, "end": v(-19.46, 74.29) * mm});
            skLineSegment(sketch, "E283", {"start": v(-19.46, 74.29) * mm, "end": v(-19.46, 102.9) * mm});
            skLineSegment(sketch, "E284", {"start": v(-19.46, 102.9) * mm, "end": v(24.85, 102.9) * mm});
            skLineSegment(sketch, "E285", {"start": v(24.85, 102.9) * mm, "end": v(24.85, 74.29) * mm});
            skLineSegment(sketch, "E286", {"start": v(24.85, 74.29) * mm, "end": v(20.84, 74.29) * mm});
            skLineSegment(sketch, "E287", {"start": v(-23.46, 163.36) * mm, "end": v(-3, 163.36) * mm});
            skLineSegment(sketch, "E288", {"start": v(-3, 163.36) * mm, "end": v(-3, 150.77) * mm});
            skLineSegment(sketch, "E289", {"start": v(7, 163.36) * mm, "end": v(7, 150.77) * mm});
            skLineSegment(sketch, "E290", {"start": v(7, 150.77) * mm, "end": v(11, 150.77) * mm});
            skLineSegment(sketch, "E291", {"start": v(11, 150.77) * mm, "end": v(11, 159.36) * mm});
            skLineSegment(sketch, "E292", {"start": v(20.85, 78.29) * mm, "end": v(20.84, 74.29) * mm});
            skLineSegment(sketch, "E293", {"start": v(2, 121.18) * mm, "end": v(2, 57.48) * mm, "construction": true});
            skPoint(sketch, "E293.startSnap0", {"position": v(2, 106.9) * mm});
            skLineSegment(sketch, "E294.bottom", {"start": v(-3, 163.36) * mm, "end": v(8, 163.36) * mm});
            skLineSegment(sketch, "E294.top", {"start": v(-3, 639.05) * mm, "end": v(8, 639.05) * mm});
            skLineSegment(sketch, "E294.left", {"start": v(-3, 163.36) * mm, "end": v(-3, 639.05) * mm});
            skLineSegment(sketch, "E294.right", {"start": v(8, 163.36) * mm, "end": v(8, 639.05) * mm});
            skSolve(sketch);
        }
        {
            var Q0;
            Q0=makeQuery(id+"F13.imprint","IMPRINT",FACE,{"disambiguationData":[TD([[makeQuery(id+"F13.imprint","IMPRINT",EDGE,{"derivedFrom":sQuery(id+"F13.wireOp",EDGE,"E264")}),-1.0]])]});
            extrude(context, id + "F14", {"entities" : qUnion([Q0]), "oppositeDirection" : true, "depth" : 1000 * mm, "offsetDistance" : 25 * mm});
        }
        {
            var Q0;
            Q0=qSketchRegion(id+"F13",true);
            extrude(context, id + "F15", {"entities" : qUnion([Q0]), "oppositeDirection" : true, "depth" : 1000 * mm, "offsetDistance" : 25 * mm});
        }
        {
            var Q0;
            Q0=makeQuery(id+"F6.opExtrude","SWEPT_FACE",FACE,{"disambiguationData":[OSD([sQuery(id+"F5.wireOp",EDGE,"E189")])]});
            var sketch = newSketch(context, id + "F16", { "sketchPlane" : qUnion([Q0])});
            skLineSegment(sketch, "E295.bottom", {"start": v(308.57, 261.27) * mm, "end": v(1308.57, 261.27) * mm});
            skLineSegment(sketch, "E295.top", {"start": v(308.57, 257.27) * mm, "end": v(1308.57, 257.27) * mm});
            skLineSegment(sketch, "E295.left", {"start": v(308.57, 261.27) * mm, "end": v(308.57, 257.27) * mm});
            skLineSegment(sketch, "E295.right", {"start": v(1308.57, 261.27) * mm, "end": v(1308.57, 257.27) * mm});
            skSolve(sketch);
        }
        {
            var Q0;
            Q0=makeQuery(id+"F16.imprint","IMPRINT",FACE,{"disambiguationData":[TD([[makeQuery(id+"F16.imprint","IMPRINT",EDGE,{"derivedFrom":sQuery(id+"F16.wireOp",EDGE,"E295.bottom")}),-1.0]])]});
            extrude(context, id + "F17", {"entities" : qUnion([Q0]), "depth" : 1700 * mm, "offsetDistance" : 25 * mm});
        }
    });
